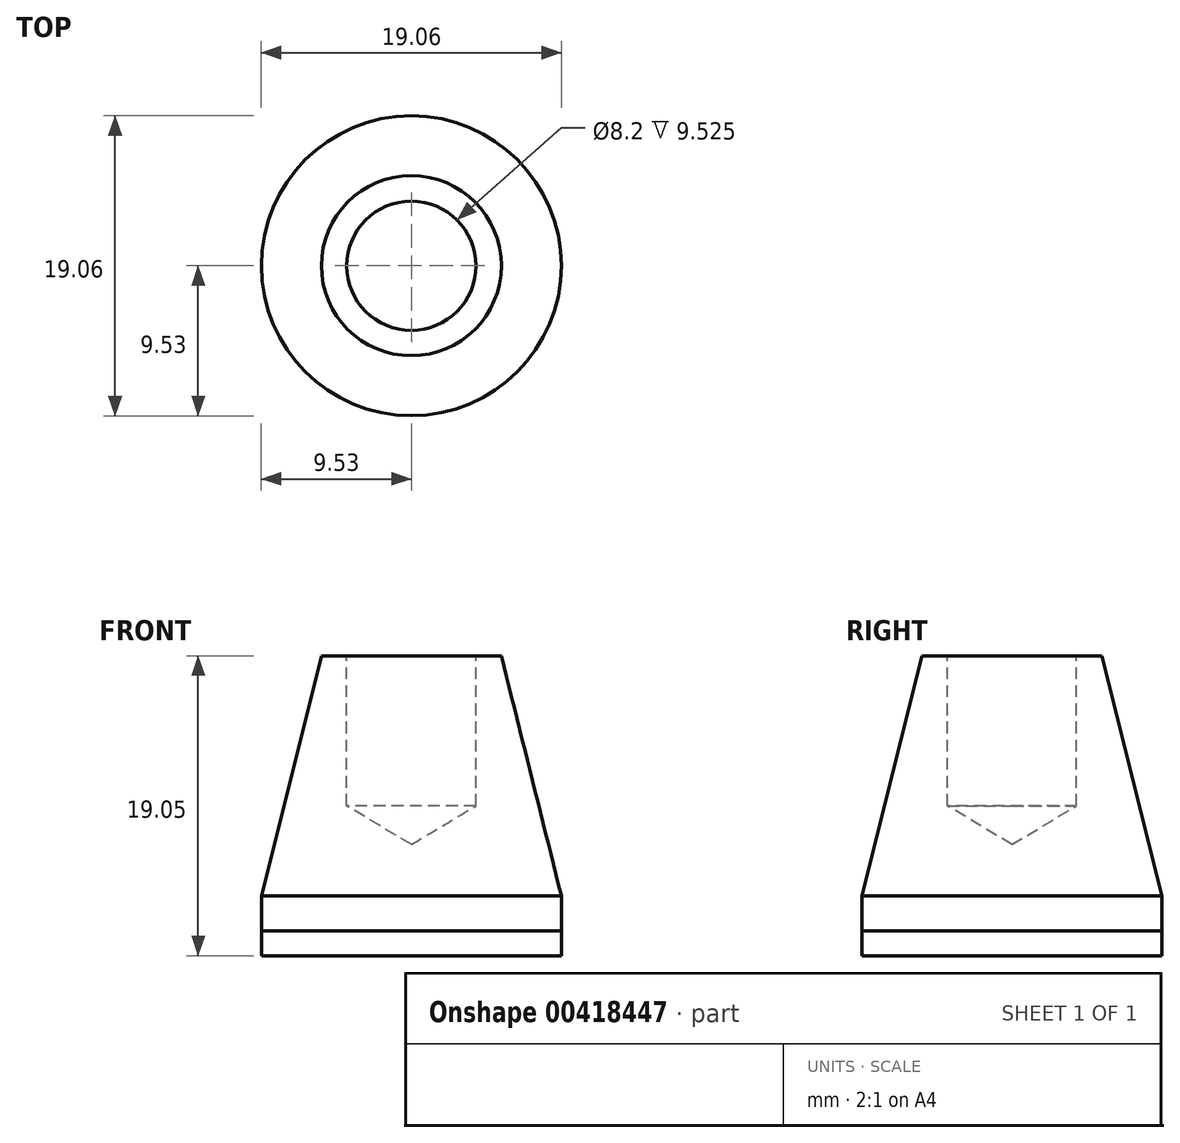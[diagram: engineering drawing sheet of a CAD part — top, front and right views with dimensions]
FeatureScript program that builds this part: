
annotation { "Feature Type Name" : "Feature", "Feature Type Description" : "" }
export const myFeature = defineFeature(function(context is Context, id is Id, definition is map)
    precondition{}
    {
        {
            var Q0;
            Q0=qCreatedBy(makeId("Top.planeOp"),FACE);
            var sketch = newSketch(context, id + "F0", { "sketchPlane" : qUnion([Q0])});
            skCircle(sketch, "E0", {"center": v(0, 0) * mm, "radius": 9.53 * mm});
            skSolve(sketch);
        }
        {
            var Q0;
            Q0=makeQuery(id+"F0.imprint","IMPRINT",FACE,{"disambiguationData":[TD([[makeQuery(id+"F0.imprint","IMPRINT",EDGE,{"derivedFrom":sQuery(id+"F0.wireOp",EDGE,"E0")}),1.0]])]});
            extrude(context, id + "F1", {"entities" : qUnion([Q0]), "oppositeDirection" : true, "depth" : 17.46 * mm});
        }
        {
            var Q0;
            Q0=makeQuery(id+"F0.imprint","IMPRINT",FACE,{"disambiguationData":[TD([[makeQuery(id+"F0.imprint","IMPRINT",EDGE,{"derivedFrom":sQuery(id+"F0.wireOp",EDGE,"E0")}),1.0]])]});
            extrude(context, id + "F2", {"entities" : qUnion([Q0]), "oppositeDirection" : true, "depth" : 19.05 * mm, "hasSecondDirection" : true, "secondDirectionOppositeDirection" : true, "secondDirectionDepth" : 17.46 * mm});
        }
        {
            var Q0;
            Q0=sQuery(id+"F0.wireOp",VERTEX,"E0.center");
            var Q1;
            Q1=makeQuery(id+"F1.opExtrude","SWEPT_BODY",BODY,{"disambiguationData":[OSD([sQuery(id+"F0.wireOp",EDGE,"E0")])]});
            hole(context, id + "F3", {"style" : HoleStyle.SIMPLE, "endStyle" : HoleEndStyle.BLIND, "standardTappedOrClearance" : lookupTablePath({ "standard" : "ANSI", "fit" : "Close", "size" : "5/16", "type" : "Clearance" }), "standardBlindInLast" : lookupTablePath({ "fit" : "Close", "standard" : "ANSI", "size" : "5/16", "type" : "Clearance" }), "holeDiameter" : 8.2 * mm, "holeDepth" : 9.52 * mm, "isTappedThrough" : true, "tappedDepth" : 12.7 * mm, "tapClearance" : 3, "startFromSketch" : true, "locations" : qUnion([Q0]), "scope" : qUnion([Q1])});
        }
        {
            var Q0;
            Q0=makeQuery(id+"F1.opExtrude","CAP_EDGE",EDGE,{"disambiguationData":[OSD([sQuery(id+"F0.wireOp",EDGE,"E0")])],"isStart":true});
            chamfer(context, id + "F4", {"entities" : qUnion([Q0]), "chamferType" : ChamferType.TWO_OFFSETS, "width1" : 15.24 * mm, "oppositeDirection" : true, "width2" : 3.8 * mm, "tangentPropagation" : true});
        }
    });
